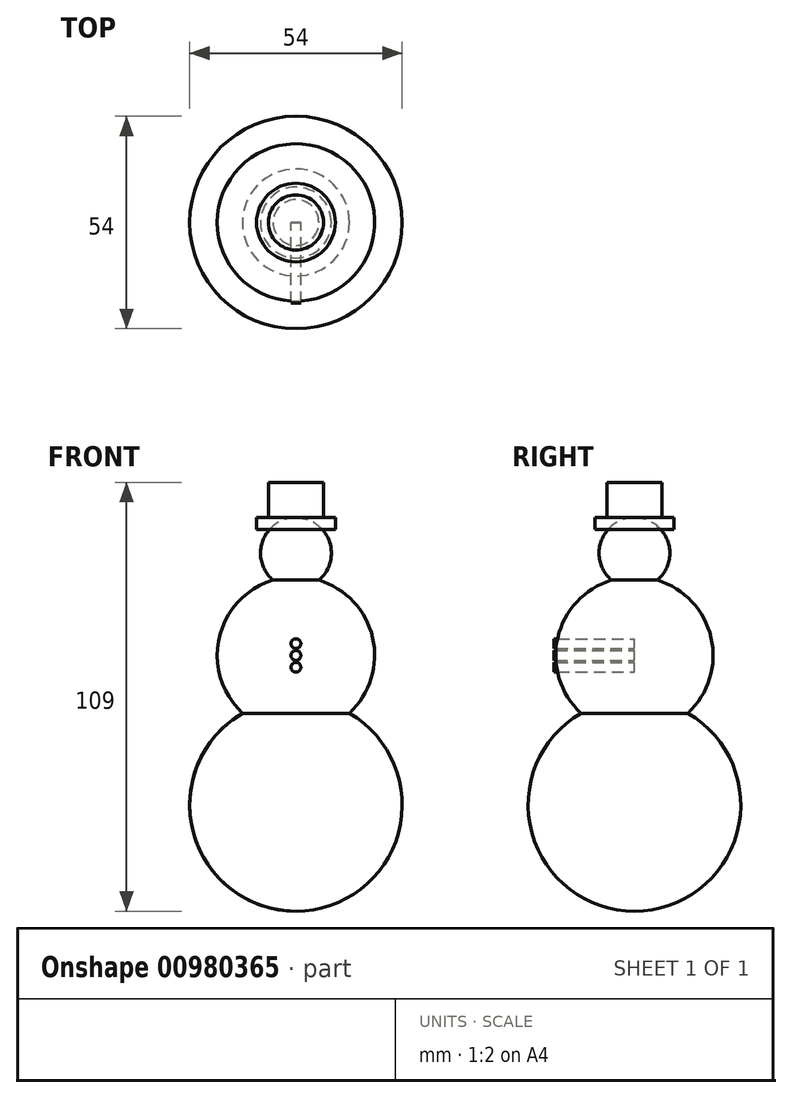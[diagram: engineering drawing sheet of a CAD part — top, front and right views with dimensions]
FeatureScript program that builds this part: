
annotation { "Feature Type Name" : "Feature", "Feature Type Description" : "" }
export const myFeature = defineFeature(function(context is Context, id is Id, definition is map)
    precondition{}
    {
        {
            var Q0;
            Q0=qCreatedBy(makeId("Front.planeOp"),FACE);
            var sketch = newSketch(context, id + "F0", { "sketchPlane" : qUnion([Q0])});
            skLineSegment(sketch, "E0", {"start": v(0, 0) * mm, "end": v(0, 100) * mm});
            skArc(sketch, "E1", {"start": v(0, 0) * mm, "mid": v(26.07, 19.96) * mm, "end": v(13.6, 50.33) * mm});
            skArc(sketch, "E2", {"start": v(13.6, 50.33) * mm, "mid": v(19.5, 69.48) * mm, "end": v(5.82, 84.13) * mm});
            skArc(sketch, "E3", {"start": v(5.82, 84.13) * mm, "mid": v(8.45, 94.1) * mm, "end": v(0, 100) * mm});
            skSolve(sketch);
        }
        {
            var Q0;
            Q0 = qSketchRegion(id + "F0", true);
            var Q1;
            Q1=sQuery(id+"F0.wireOp",EDGE,"E0");
            revolve(context, id + "F1", {"surfaceOperationType" : NewSurfaceOperationType.NEW, "entities" : qUnion([Q0]), "axis" : qUnion([Q1]), "revolveType" : RevolveType.FULL});
        }
        {
            var Q0;
            Q0=qCreatedBy(makeId("Front.planeOp"),FACE);
            var sketch = newSketch(context, id + "F2", { "sketchPlane" : qUnion([Q0])});
            skLineSegment(sketch, "E4", {"start": v(0, 0) * mm, "end": v(0, 109) * mm});
            skLineSegment(sketch, "E5", {"start": v(0, 109) * mm, "end": v(7, 109) * mm});
            skLineSegment(sketch, "E6", {"start": v(7, 109) * mm, "end": v(7, 100) * mm});
            skLineSegment(sketch, "E7", {"start": v(7, 100) * mm, "end": v(10, 100) * mm});
            skLineSegment(sketch, "E8", {"start": v(10, 100) * mm, "end": v(10, 97) * mm});
            skLineSegment(sketch, "E9", {"start": v(10, 97) * mm, "end": v(0, 97) * mm});
            skSolve(sketch);
        }
        {
            var Q0;
            Q0 = qSketchRegion(id + "F2", true);
            var Q1;
            Q1=sQuery(id+"F2.wireOp",EDGE,"E4");
            revolve(context, id + "F3", {"surfaceOperationType" : NewSurfaceOperationType.NEW, "entities" : qUnion([Q0]), "axis" : qUnion([Q1]), "revolveType" : RevolveType.FULL});
        }
        {
            var Q0;
            Q0=qCreatedBy(makeId("Front.planeOp"),FACE);
            var sketch = newSketch(context, id + "F4", { "sketchPlane" : qUnion([Q0])});
            skCircle(sketch, "E10", {"center": v(0, 68) * mm, "radius": 1.25 * mm});
            skCircle(sketch, "E11.0.1.0", {"center": v(0, 65) * mm, "radius": 1.25 * mm});
            skCircle(sketch, "E11.0.2.0", {"center": v(0, 62) * mm, "radius": 1.25 * mm});
            skSolve(sketch);
        }
        {
            var Q0;
            Q0 = qSketchRegion(id + "F4", true);
            extrude(context, id + "F5", {"entities" : qUnion([Q0]), "depth" : 20.5 * mm, "offsetDistance" : 25 * mm});
        }
    });
